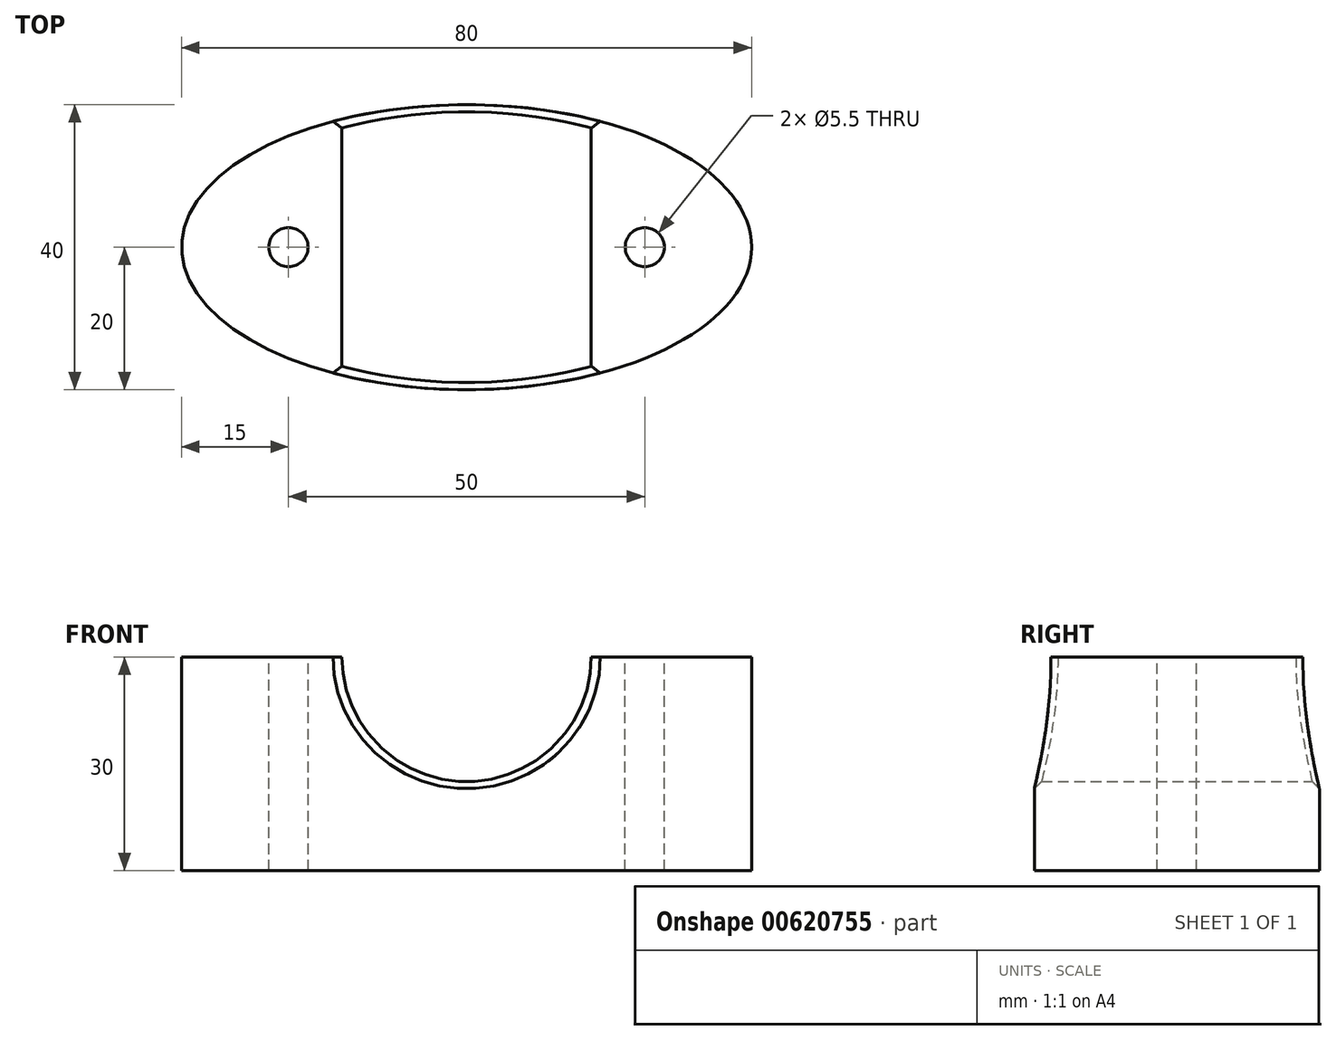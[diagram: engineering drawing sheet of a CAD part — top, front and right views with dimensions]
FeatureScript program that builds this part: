
annotation { "Feature Type Name" : "Feature", "Feature Type Description" : "" }
export const myFeature = defineFeature(function(context is Context, id is Id, definition is map)
    precondition{}
    {
        {
            var Q0;
            Q0=qCreatedBy(makeId("Top.planeOp"),FACE);
            var sketch = newSketch(context, id + "F0", { "sketchPlane" : qUnion([Q0])});
            skEllipse(sketch, "E0", {"center": v(-455.43, 0) * mm, "majorRadius": 40 * mm, "minorRadius": 20 * mm, "majorAxis": v(1, 0)});
            skSolve(sketch);
        }
        {
            var Q0;
            Q0=makeQuery(id+"F0.imprint","IMPRINT",FACE,{"disambiguationData":[TD([[makeQuery(id+"F0.imprint","IMPRINT",EDGE,{"derivedFrom":sQuery(id+"F0.wireOp",EDGE,"E0")}),1.0]])]});
            extrude(context, id + "F1", {"entities" : qUnion([Q0]), "depth" : 30 * mm, "offsetDistance" : 25 * mm});
        }
        {
            var Q0;
            Q0=makeQuery(id+"F1.opExtrude","CAP_FACE",FACE,{"disambiguationData":[OSD([sQuery(id+"F0.wireOp",EDGE,"E0")])],"isStart":false});
            var sketch = newSketch(context, id + "F2", { "sketchPlane" : qUnion([Q0])});
            skLineSegment(sketch, "E1", {"start": v(-455.43, 0) * mm, "end": v(-430.43, 0) * mm});
            skLineSegment(sketch, "E2", {"start": v(-455.43, 0) * mm, "end": v(-480.43, 0) * mm});
            skSolve(sketch);
        }
        {
            var Q0;
            Q0=sQuery(id+"F2.wireOp",VERTEX,"E2.end");
            var Q1;
            Q1=sQuery(id+"F2.wireOp",VERTEX,"E1.end");
            var Q2;
            Q2=makeQuery(id+"F1.opExtrude","SWEPT_BODY",BODY,{"disambiguationData":[OSD([sQuery(id+"F0.wireOp",EDGE,"E0")])]});
            hole(context, id + "F3", {"style" : HoleStyle.SIMPLE, "endStyle" : HoleEndStyle.THROUGH, "standardTappedOrClearance" : lookupTablePath({ "standard" : "ISO", "fit" : "Normal", "size" : "M5", "type" : "Clearance" }), "standardBlindInLast" : lookupTablePath({ "fit" : "Standard", "standard" : "ISO", "size" : "M5", "type" : "Clearance" }), "holeDiameter" : 5.5 * mm, "majorDiameter" : 5 * mm, "isTappedThrough" : true, "tappedDepth" : 12 * mm, "tapClearance" : 3, "locations" : qUnion([Q0, Q1]), "scope" : qUnion([Q2])});
        }
        {
            var Q0;
            Q0=qCreatedBy(makeId("Front.planeOp"),FACE);
            var sketch = newSketch(context, id + "F4", { "sketchPlane" : qUnion([Q0])});
            skCircle(sketch, "E3", {"center": v(-455.43, 30) * mm, "radius": 17.5 * mm});
            skLineSegment(sketch, "E4", {"start": v(-433.18, 30) * mm, "end": v(-477.68, 30) * mm});
            skLineSegment(sketch, "E5", {"start": v(-483.18, 30) * mm, "end": v(-495.43, 30) * mm});
            skLineSegment(sketch, "E6", {"start": v(-415.43, 30) * mm, "end": v(-427.68, 30) * mm});
            skSolve(sketch);
        }
        {
            var Q0;
            {var subQ0=sQuery(id+"F4.wireOp",EDGE,"E4");var subQ1=sQuery(id+"F4.wireOp",EDGE,"E3");var subQ2=makeQuery(id+"F4.imprint","INTERSECT",VERTEX,{"disambiguationData":[OD(0.0)],"derivedFrom":[subQ1,subQ0]});Q0=makeQuery(id+"F4.imprint","IMPRINT",FACE,{"disambiguationData":[TD([[makeQuery(id+"F4.imprint","IMPRINT",EDGE,{"disambiguationData":[TD([[subQ2,-1.0]])],"derivedFrom":subQ1}),1.0]])]});}
            var Q1;
            Q1=sQuery(id+"F4.wireOp",EDGE,"E3");
            extrude(context, id + "F5", {"entities" : qUnion([Q0]), "operationType" : NewBodyOperationType.REMOVE, "surfaceEntities" : qUnion([Q1]), "depth" : 25 * mm, "offsetDistance" : 25 * mm});
        }
        {
            var Q0;
            Q0=makeQuery(id+"F5.boolean.opBoolean","COPY",FACE,{"derivedFrom":makeQuery(id+"F5.opExtrude","CAP_FACE",FACE,{"disambiguationData":[OSD([sQuery(id+"F4.wireOp",EDGE,"E3"),sQuery(id+"F4.wireOp",EDGE,"E4")])],"isStart":true})});
            var Q1;
            Q1=sQuery(id+"F4.wireOp",EDGE,"E3");
            var Q2;
            Q2=sQuery(id+"F4.wireOp",EDGE,"E4");
            extrude(context, id + "F6", {"entities" : qUnion([Q0]), "operationType" : NewBodyOperationType.REMOVE, "surfaceEntities" : qUnion([Q1, Q2]), "oppositeDirection" : true, "depth" : 25 * mm, "offsetDistance" : 25 * mm});
        }
        {
            var Q0;
            Q0=makeQuery(id+"F5.boolean.opBoolean","INTERSECT",EDGE,{"derivedFrom":[makeQuery(id+"F1.opExtrude","SWEPT_FACE",FACE,{"disambiguationData":[OSD([sQuery(id+"F0.wireOp",EDGE,"E0")])]}),makeQuery(id+"F5.opExtrude","SWEPT_FACE",FACE,{"disambiguationData":[OSD([sQuery(id+"F4.wireOp",EDGE,"E3")])]})]});
            var Q1;
            Q1=makeQuery(id+"F6.boolean.opBoolean","INTERSECT",EDGE,{"derivedFrom":[makeQuery(id+"F1.opExtrude","SWEPT_FACE",FACE,{"disambiguationData":[OSD([sQuery(id+"F0.wireOp",EDGE,"E0")])]}),makeQuery(id+"F6.opExtrude","SWEPT_FACE",FACE,{"disambiguationData":[OSD([sQuery(id+"F4.wireOp",EDGE,"E3")])]})]});
            chamfer(context, id + "F7", {"entities" : qUnion([Q0, Q1]), "width" : 1 * mm, "tangentPropagation" : true});
        }
    });
